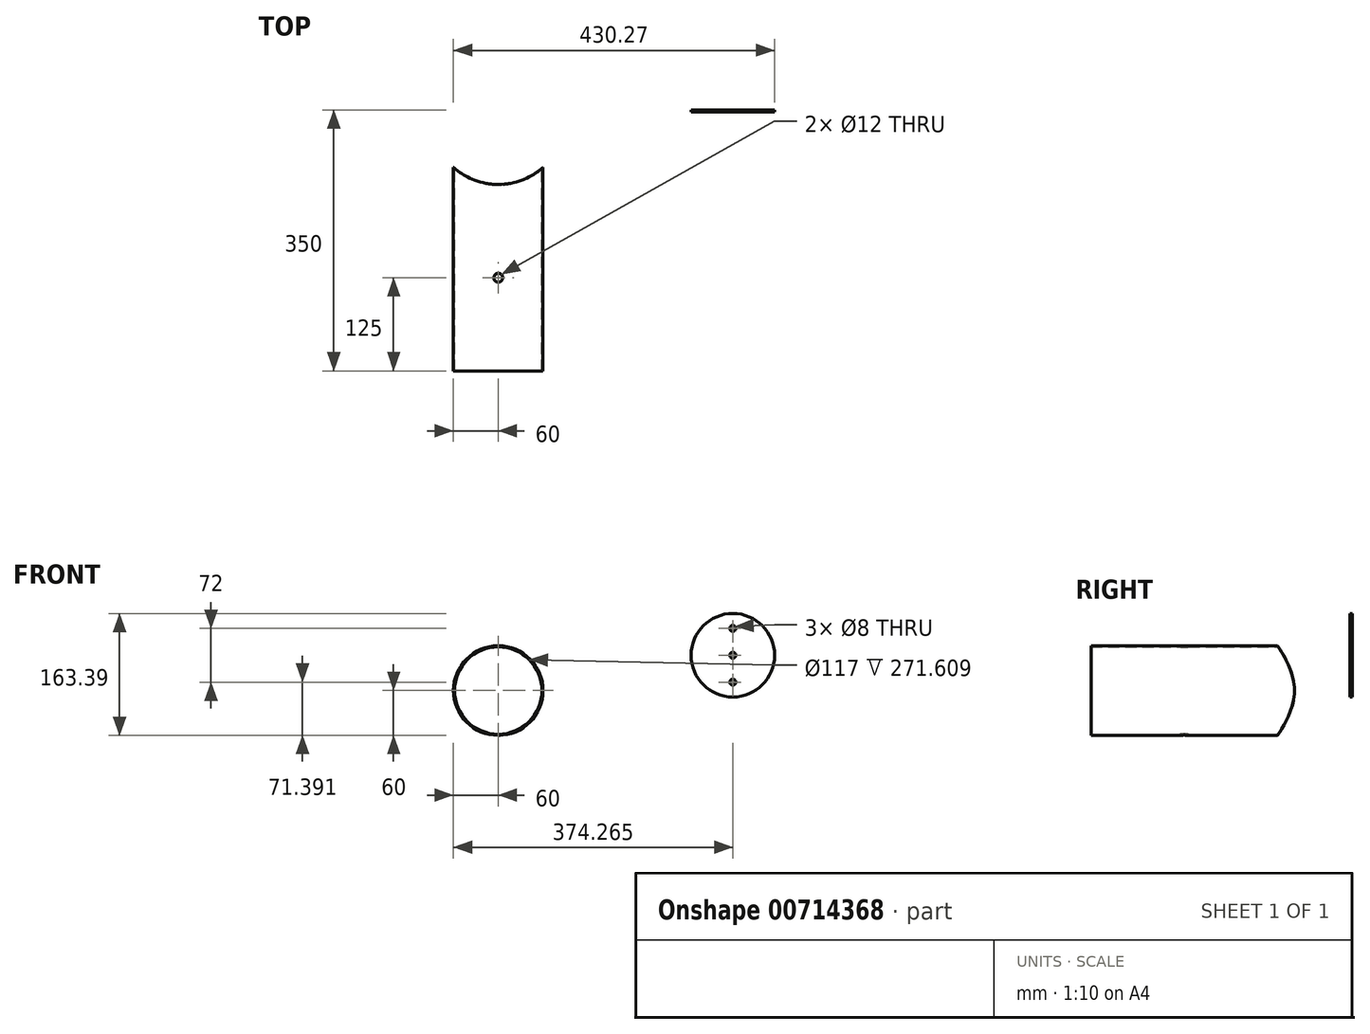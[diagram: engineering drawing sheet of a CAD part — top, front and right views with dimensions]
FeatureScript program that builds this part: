
annotation { "Feature Type Name" : "Feature", "Feature Type Description" : "" }
export const myFeature = defineFeature(function(context is Context, id is Id, definition is map)
    precondition{}
    {
        {
            var Q0;
            Q0=qCreatedBy(makeId("Front.planeOp"),FACE);
            var sketch = newSketch(context, id + "F0", { "sketchPlane" : qUnion([Q0])});
            skCircle(sketch, "E0", {"center": v(0, 0) * mm, "radius": 60 * mm});
            skCircle(sketch, "E1.0", {"center": v(0, 0) * mm, "radius": 58.5 * mm});
            skSolve(sketch);
        }
        {
            var Q0;
            Q0=makeQuery(id+"F0.imprint","IMPRINT",FACE,{"disambiguationData":[TD([[makeQuery(id+"F0.imprint","IMPRINT",EDGE,{"derivedFrom":sQuery(id+"F0.wireOp",EDGE,"E0")}),1.0]])]});
            extrude(context, id + "F1", {"entities" : qUnion([Q0]), "depth" : 350 * mm, "offsetDistance" : 25 * mm});
        }
        {
            var Q0;
            Q0=qCreatedBy(makeId("Top.planeOp"),FACE);
            var sketch = newSketch(context, id + "F2", { "sketchPlane" : qUnion([Q0])});
            skCircle(sketch, "E2", {"center": v(0, -10) * mm, "radius": 90 * mm});
            skSolve(sketch);
        }
        {
            var Q0;
            Q0=makeQuery(id+"F2.imprint","IMPRINT",FACE,{"disambiguationData":[TD([[makeQuery(id+"F2.imprint","IMPRINT",EDGE,{"derivedFrom":sQuery(id+"F2.wireOp",EDGE,"E2")}),1.0]])]});
            extrude(context, id + "F3", {"entities" : qUnion([Q0]), "operationType" : NewBodyOperationType.REMOVE, "endBound" : BoundingType.SYMMETRIC, "oppositeDirection" : true, "depth" : 120 * mm, "offsetDistance" : 25 * mm});
        }
        {
            var Q0;
            Q0=qCreatedBy(makeId("Top.planeOp"),FACE);
            var sketch = newSketch(context, id + "F4", { "sketchPlane" : qUnion([Q0])});
            skCircle(sketch, "E3", {"center": v(0, -225) * mm, "radius": 6 * mm});
            skSolve(sketch);
        }
        {
            var Q0;
            Q0=makeQuery(id+"F4.imprint","IMPRINT",FACE,{"disambiguationData":[TD([[makeQuery(id+"F4.imprint","IMPRINT",EDGE,{"derivedFrom":sQuery(id+"F4.wireOp",EDGE,"E3")}),1.0]])]});
            extrude(context, id + "F5", {"entities" : qUnion([Q0]), "operationType" : NewBodyOperationType.REMOVE, "endBound" : BoundingType.SYMMETRIC, "oppositeDirection" : true, "depth" : 120 * mm, "offsetDistance" : 25 * mm});
        }
        {
            var Q0;
            Q0=qCreatedBy(makeId("Front.planeOp"),FACE);
            var sketch = newSketch(context, id + "F6", { "sketchPlane" : qUnion([Q0])});
            skCircle(sketch, "E4", {"center": v(314.27, 47.4) * mm, "radius": 56 * mm});
            skLineSegment(sketch, "E5", {"start": v(314.27, 47.4) * mm, "end": v(314.27, 103.4) * mm, "construction": true});
            skLineSegment(sketch, "E6", {"start": v(314.27, 103.4) * mm, "end": v(314.27, -8.6) * mm, "construction": true});
            skCircle(sketch, "E7", {"center": v(314.27, 83.4) * mm, "radius": 4 * mm});
            skCircle(sketch, "E8", {"center": v(314.27, 47.4) * mm, "radius": 4 * mm});
            skCircle(sketch, "E9", {"center": v(314.27, 11.4) * mm, "radius": 4 * mm});
            skSolve(sketch);
        }
        {
            var Q0;
            Q0=makeQuery(id+"F6.imprint","IMPRINT",FACE,{"disambiguationData":[TD([[makeQuery(id+"F6.imprint","IMPRINT",EDGE,{"derivedFrom":sQuery(id+"F6.wireOp",EDGE,"E4")}),1.0]])]});
            extrude(context, id + "F7", {"entities" : qUnion([Q0]), "depth" : 3 * mm, "offsetDistance" : 25 * mm});
        }
    });
